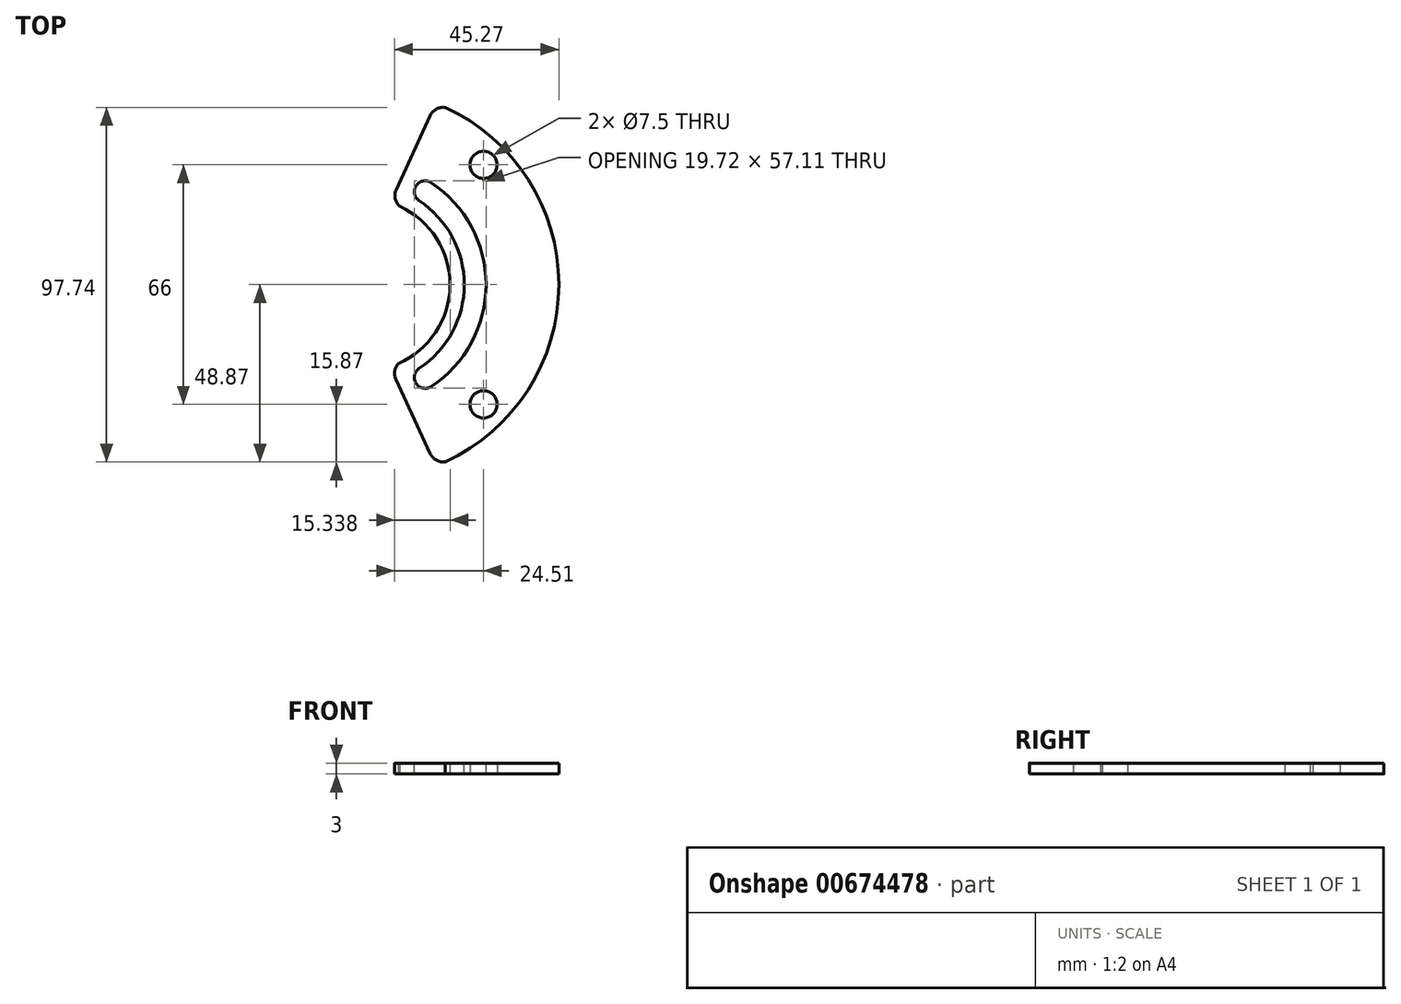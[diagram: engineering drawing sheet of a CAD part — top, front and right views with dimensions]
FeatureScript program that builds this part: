
annotation { "Feature Type Name" : "Feature", "Feature Type Description" : "" }
export const myFeature = defineFeature(function(context is Context, id is Id, definition is map)
    precondition{}
    {
        {
            var Q0;
            Q0=qCreatedBy(makeId("Top.planeOp"),FACE);
            var sketch = newSketch(context, id + "F0", { "sketchPlane" : qUnion([Q0])});
            skCircle(sketch, "E0", {"center": v(0, 0) * mm, "radius": 46.67 * mm, "construction": true});
            skLineSegment(sketch, "E1", {"start": v(0, 0) * mm, "end": v(33, 33) * mm, "construction": true});
            skCircle(sketch, "E2", {"center": v(33, 33) * mm, "radius": 3.75 * mm});
            skCircle(sketch, "E3.1.0", {"center": v(-33, 33) * mm, "radius": 3.75 * mm});
            skCircle(sketch, "E3.2.0", {"center": v(-33, -33) * mm, "radius": 3.75 * mm});
            skCircle(sketch, "E3.3.0", {"center": v(33, -33) * mm, "radius": 3.75 * mm});
            skLineSegment(sketch, "E4", {"start": v(0, 0) * mm, "end": v(33, -33) * mm, "construction": true});
            skSolve(sketch);
        }
        {
            var Q0;
            Q0=qCreatedBy(makeId("Top.planeOp"),FACE);
            var sketch = newSketch(context, id + "F1", { "sketchPlane" : qUnion([Q0])});
            skLineSegment(sketch, "E5", {"start": v(8.94, 26.26) * mm, "end": v(18.3, 46.55) * mm});
            skLineSegment(sketch, "E6", {"start": v(8.86, -26.1) * mm, "end": v(18.3, -46.55) * mm});
            skLineSegment(sketch, "E7", {"start": v(0, 0) * mm, "end": v(0, 47.02) * mm, "construction": true});
            skLineSegment(sketch, "E8", {"start": v(0, 0) * mm, "end": v(0, -26.99) * mm, "construction": true});
            skPoint(sketch, "E9.visualSharp", {"position": v(17.93, 45.77) * mm});
            skArc(sketch, "E9.filletArc", {"start": v(22.48, 48.83) * mm, "mid": v(20, 48.38) * mm, "end": v(18.3, 46.55) * mm});
            skPoint(sketch, "E10.visualSharp", {"position": v(5.23, 18.21) * mm});
            skArc(sketch, "E10.filletArc", {"start": v(8.94, 26.26) * mm, "mid": v(8.66, 23.76) * mm, "end": v(9.92, 21.59) * mm});
            skPoint(sketch, "E11.visualSharp", {"position": v(5.23, -18.21) * mm});
            skArc(sketch, "E11.filletArc", {"start": v(10.82, -20.78) * mm, "mid": v(8.74, -23.03) * mm, "end": v(8.86, -26.1) * mm});
            skPoint(sketch, "E12.visualSharp", {"position": v(17.93, -45.77) * mm});
            skArc(sketch, "E12.filletArc", {"start": v(18.3, -46.55) * mm, "mid": v(20, -48.38) * mm, "end": v(22.48, -48.83) * mm});
            skArc(sketch, "E13", {"start": v(9.92, 21.59) * mm, "mid": v(20, 12.82) * mm, "end": v(23.76, 0) * mm});
            skArc(sketch, "E14", {"start": v(23.76, 0) * mm, "mid": v(19.87, -13.03) * mm, "end": v(9.48, -21.79) * mm});
            skArc(sketch, "E15", {"start": v(22.48, 48.83) * mm, "mid": v(45.27, 29) * mm, "end": v(53.76, 0) * mm});
            skArc(sketch, "E16", {"start": v(53.76, 0) * mm, "mid": v(45.27, -29) * mm, "end": v(22.48, -48.83) * mm});
            skSolve(sketch);
        }
        {
            var Q0;
            Q0=makeQuery(id+"F1.imprint","IMPRINT",FACE,{"disambiguationData":[TD([[makeQuery(id+"F1.imprint","IMPRINT",EDGE,{"derivedFrom":sQuery(id+"F1.wireOp",EDGE,"E5")}),-1.0]])]});
            extrude(context, id + "F2", {"entities" : qUnion([Q0]), "depth" : 3 * mm, "offsetDistance" : 25 * mm});
        }
        {
            var Q0;
            Q0=makeQuery(id+"F0.imprint","IMPRINT",FACE,{"disambiguationData":[TD([[makeQuery(id+"F0.imprint","IMPRINT",EDGE,{"derivedFrom":sQuery(id+"F0.wireOp",EDGE,"E2")}),1.0]])]});
            var Q1;
            Q1=makeQuery(id+"F0.imprint","IMPRINT",FACE,{"disambiguationData":[TD([[makeQuery(id+"F0.imprint","IMPRINT",EDGE,{"derivedFrom":sQuery(id+"F0.wireOp",EDGE,"E3.3.0")}),1.0]])]});
            extrude(context, id + "F3", {"entities" : qUnion([Q0, Q1]), "operationType" : NewBodyOperationType.REMOVE, "depth" : 25 * mm, "offsetDistance" : 25 * mm});
        }
        {
            var Q0;
            Q0=makeQuery(id+"F2.opExtrude","CAP_FACE",FACE,{"disambiguationData":[OSD([sQuery(id+"F1.wireOp",EDGE,"KiuFZQME-wWnU-ktu5-Gd9x-qji5TMNZz2fd"),sQuery(id+"F1.wireOp",EDGE,"G5eraXv0-ftC7-V2Hx-4i3N-1R2XA50WnSdq"),sQuery(id+"F1.wireOp",EDGE,"E5"),sQuery(id+"F1.wireOp",EDGE,"E6"),sQuery(id+"F1.wireOp",EDGE,"57560024-62e8-479f-91f4-8b403f4d0ad7.filletArc"),sQuery(id+"F1.wireOp",EDGE,"ddf71622-e854-4fa8-aca5-087326283111.filletArc"),sQuery(id+"F1.wireOp",EDGE,"85b82a5b-4425-4996-801d-5779b438c59f.filletArc"),sQuery(id+"F1.wireOp",EDGE,"35c327b1-5974-4460-b54d-dc77ba413df5.filletArc")])],"isStart":false});
            var sketch = newSketch(context, id + "F4", { "sketchPlane" : qUnion([Q0])});
            skArc(sketch, "E17", {"start": v(15.26, 23.1) * mm, "mid": v(27.69, 0) * mm, "end": v(15.26, -23.1) * mm});
            skArc(sketch, "E18", {"start": v(18.57, 28.11) * mm, "mid": v(33.69, 0) * mm, "end": v(18.57, -28.11) * mm});
            skLineSegment(sketch, "E19", {"start": v(0, 0) * mm, "end": v(18.57, -28.11) * mm, "construction": true});
            skLineSegment(sketch, "E20", {"start": v(0, 0) * mm, "end": v(18.57, 28.11) * mm, "construction": true});
            skLineSegment(sketch, "E21", {"start": v(15.26, 23.1) * mm, "end": v(15.26, 0) * mm, "construction": true});
            skLineSegment(sketch, "E22", {"start": v(15.26, 0) * mm, "end": v(15.26, -23.1) * mm, "construction": true});
            skArc(sketch, "E23", {"start": v(15.26, 23.1) * mm, "mid": v(14.41, 27.26) * mm, "end": v(18.57, 28.11) * mm});
            skArc(sketch, "E24", {"start": v(15.26, -23.1) * mm, "mid": v(14.41, -27.26) * mm, "end": v(18.57, -28.11) * mm});
            skSolve(sketch);
        }
        {
            var Q0;
            Q0 = qSketchRegion(id + "F4", true);
            extrude(context, id + "F5", {"entities" : qUnion([Q0]), "operationType" : NewBodyOperationType.REMOVE, "oppositeDirection" : true, "depth" : 25 * mm, "offsetDistance" : 25 * mm});
        }
    });
